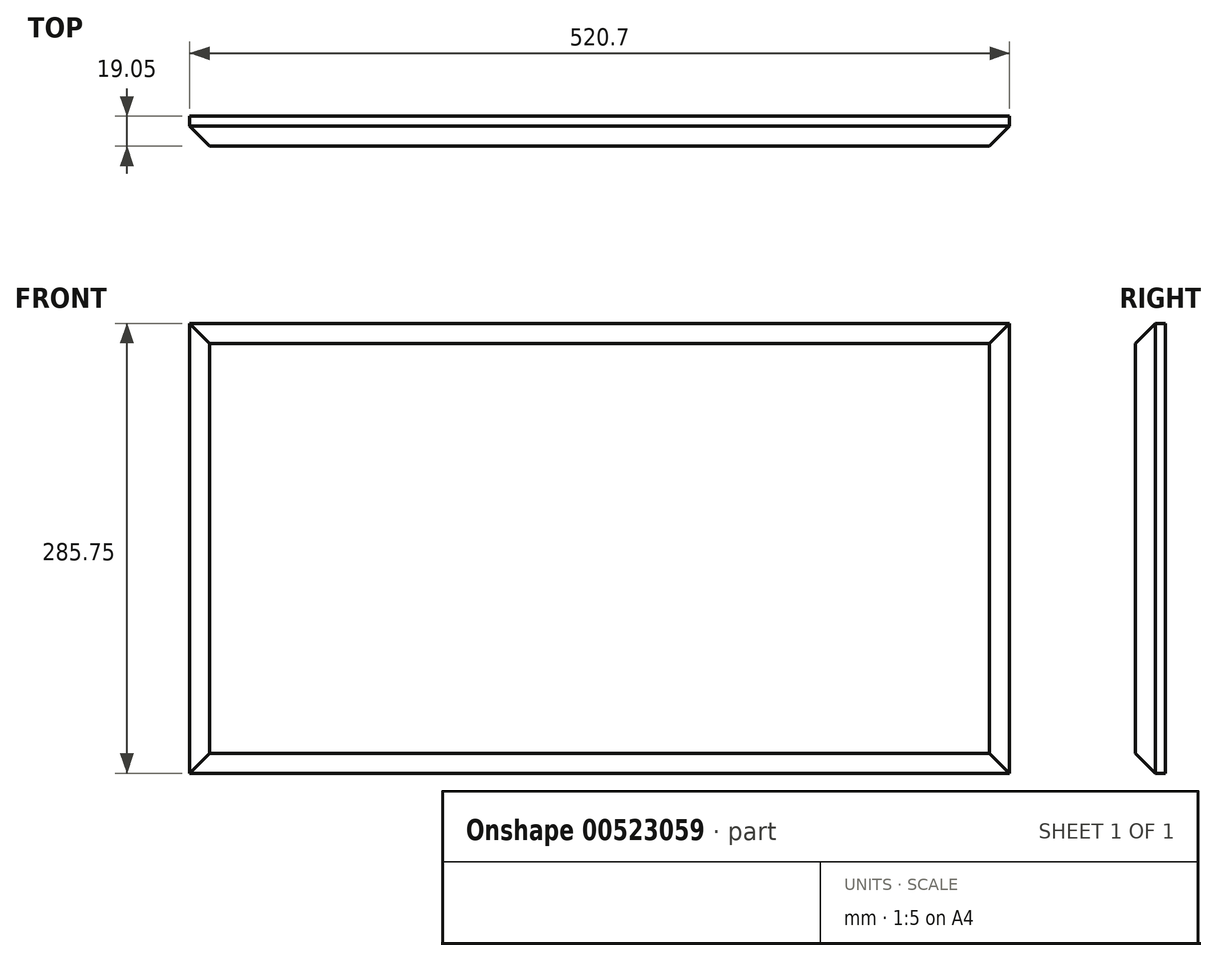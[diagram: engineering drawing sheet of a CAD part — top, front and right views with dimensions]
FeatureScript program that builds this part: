
annotation { "Feature Type Name" : "Feature", "Feature Type Description" : "" }
export const myFeature = defineFeature(function(context is Context, id is Id, definition is map)
    precondition{}
    {
        {
            var Q0;
            Q0=qCreatedBy(makeId("Front.planeOp"),FACE);
            var sketch = newSketch(context, id + "F0", { "sketchPlane" : qUnion([Q0])});
            skLineSegment(sketch, "E0.bottom", {"start": v(0, 0) * mm, "end": v(520.7, 0) * mm});
            skLineSegment(sketch, "E0.top", {"start": v(0, 285.75) * mm, "end": v(520.7, 285.75) * mm});
            skLineSegment(sketch, "E0.left", {"start": v(0, 0) * mm, "end": v(0, 285.75) * mm});
            skLineSegment(sketch, "E0.right", {"start": v(520.7, 0) * mm, "end": v(520.7, 285.75) * mm});
            skSolve(sketch);
        }
        {
            var Q0;
            Q0 = qSketchRegion(id + "F0", true);
            extrude(context, id + "F1", {"entities" : qUnion([Q0]), "depth" : 19.05 * mm, "offsetDistance" : 25.4 * mm});
        }
        {
            var Q0;
            Q0=makeQuery(id+"F1.opExtrude","CAP_FACE",FACE,{"disambiguationData":[OSD([sQuery(id+"F0.wireOp",EDGE,"E0.bottom"),sQuery(id+"F0.wireOp",EDGE,"E0.top"),sQuery(id+"F0.wireOp",EDGE,"E0.left"),sQuery(id+"F0.wireOp",EDGE,"E0.right")])],"isStart":false});
            chamfer(context, id + "F2", {"entities" : qUnion([Q0]), "width" : 12.7 * mm, "tangentPropagation" : true});
        }
    });
